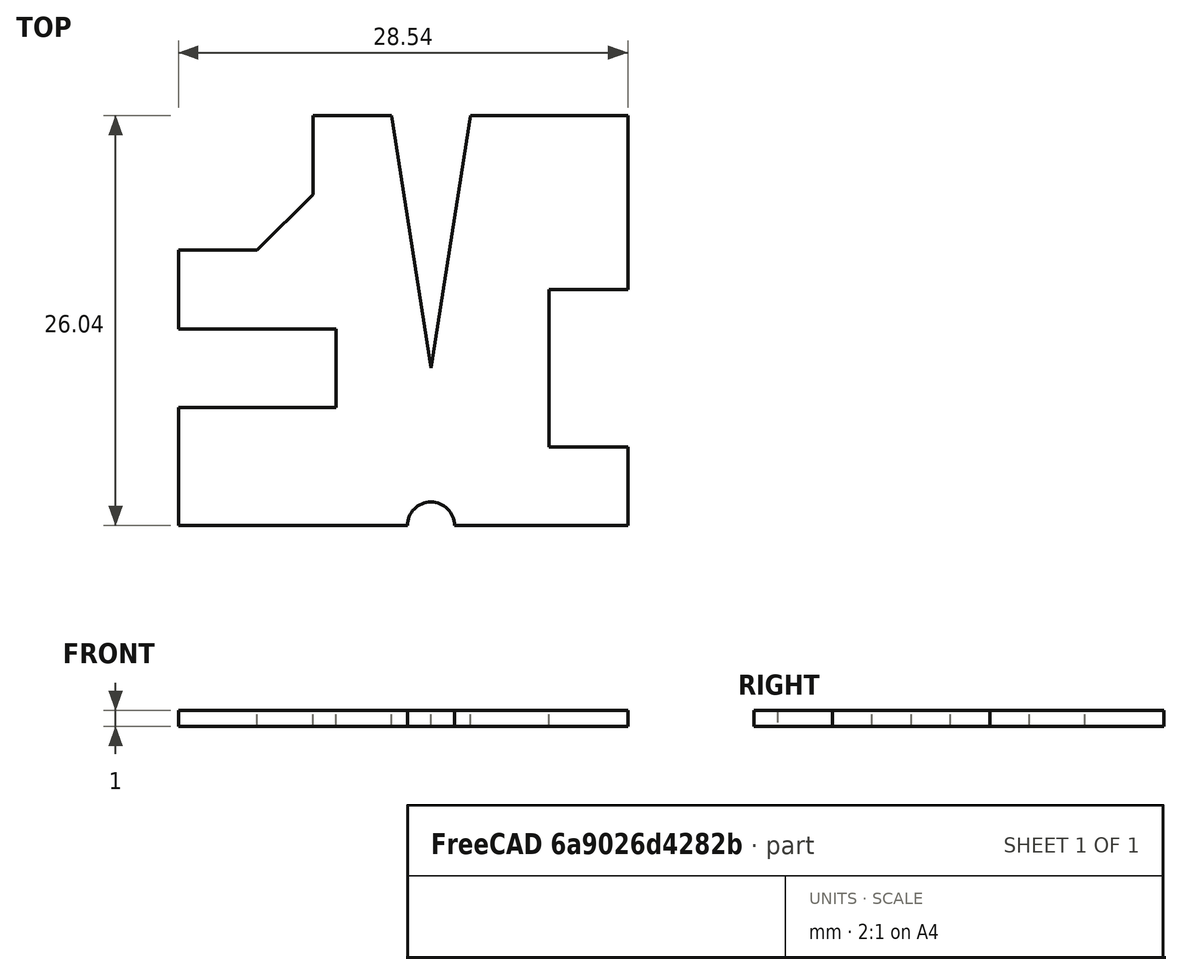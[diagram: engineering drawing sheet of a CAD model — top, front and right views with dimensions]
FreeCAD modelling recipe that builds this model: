
FCSTD DOCUMENT  (FreeCAD 0.19R16203 (Git))
Label: DogBone
License: CreativeCommons Attribution
LicenseURL: http://creativecommons.org/licenses/by/4.0/
objects: Sketcher::SketchObject×1, PartDesign::Pad×1, PartDesign::Body×1
note: 4 computed .brp shape members not serialized (recipe doc carries the construction recipe); baked Part::Feature solids carry a one-line shape summary decoded from their .brp

FEATURE [Sketcher::SketchObject] Sketch
  MapMode = 5
  Support = -> [XY_Plane001]
  sketch-geometry (20):
    g0: LineSegment StartX=-16.0355 StartY=-10 StartZ=0 EndX=-16.0355 EndY=-2.5 EndZ=0
    g1: LineSegment StartX=-16.0355 StartY=-2.5 StartZ=0 EndX=-6.03553 EndY=-2.5 EndZ=0
    g2: LineSegment StartX=-6.03553 StartY=-2.5 StartZ=0 EndX=-6.03553 EndY=2.5 EndZ=0
    g3: LineSegment StartX=-6.03553 StartY=2.5 StartZ=0 EndX=-16.0355 EndY=2.5 EndZ=0
    g4: LineSegment StartX=-16.0355 StartY=2.5 StartZ=0 EndX=-16.0355 EndY=7.5 EndZ=0
    g5: LineSegment StartX=-16.0355 StartY=7.5 StartZ=0 EndX=-11.0355 EndY=7.5 EndZ=0
    g6: LineSegment StartX=-11.0355 StartY=7.5 StartZ=0 EndX=-7.5 EndY=11.0355 EndZ=0
    g7: LineSegment StartX=-7.5 StartY=11.0355 StartZ=0 EndX=-7.5 EndY=16.0355 EndZ=0
    g8: LineSegment StartX=-7.5 StartY=16.0355 StartZ=0 EndX=-2.5 EndY=16.0355 EndZ=0
    g9: LineSegment StartX=-2.5 StartY=16.0355 StartZ=0 EndX=0 EndY=0 EndZ=0
    g10: LineSegment StartX=0 StartY=0 StartZ=0 EndX=2.5 EndY=16.0355 EndZ=0
    g11: LineSegment StartX=2.5 StartY=16.0355 StartZ=0 EndX=12.5 EndY=16.0355 EndZ=0
    g12: LineSegment StartX=12.5 StartY=16.0355 StartZ=0 EndX=12.5 EndY=5 EndZ=0
    g13: LineSegment StartX=12.5 StartY=5 StartZ=0 EndX=7.5 EndY=5 EndZ=0
    g14: LineSegment StartX=7.5 StartY=5 StartZ=0 EndX=7.5 EndY=-5 EndZ=0
    g15: LineSegment StartX=7.5 StartY=-5 StartZ=0 EndX=12.5 EndY=-5 EndZ=0
    g16: LineSegment StartX=12.5 StartY=-5 StartZ=0 EndX=12.5 EndY=-10 EndZ=0
    g17: LineSegment StartX=12.5 StartY=-10 StartZ=0 EndX=1.5 EndY=-10 EndZ=0
    g18: LineSegment StartX=-1.5 StartY=-10 StartZ=0 EndX=-16.0355 EndY=-10 EndZ=0
    g19: ArcOfCircle CenterX=0 CenterY=-10 CenterZ=0 NormalX=0 NormalY=0 NormalZ=1 AngleXU=0 Radius=1.5 StartAngle=0 EndAngle=3.14159
  constraints (57):
    c: Vertical(g0)
    c: Coincident(g0,g1)
    c: Horizontal(g1)
    c: Coincident(g1,g2)
    c: Coincident(g2,g3)
    c: Horizontal(g3)
    c: Coincident(g3,g4)
    c: Vertical(g4)
    c: Coincident(g4,g5)
    c: Horizontal(g5)
    c: Coincident(g5,g6)
    c: Coincident(g6,g7)
    c: Vertical(g7)
    c: Coincident(g7,g8)
    c: Horizontal(g8)
    c: Coincident(g8,g9)
    c: Coincident(g9,g10)
    c: Coincident(g10,g11)
    c: Horizontal(g11)
    c: Coincident(g11,g12)
    c: Vertical(g12)
    c: Coincident(g12,g13)
    c: Coincident(g13,g14)
    c: Coincident(g14,g15)
    c: Horizontal(g15)
    c: Coincident(g15,g16)
    c: Vertical(g16)
    c: Coincident(g18,g0)
    c: Horizontal(g13)
    c: Equal(g13,g15)
    c: Symmetric(g13,g14,g-1)
    c: Symmetric(g8,g10,g-2)
    c: Equal(g3,g1)
    c: Symmetric(g3,g0,g-1)
    c: DistanceX(g15,g15) = 5
    c: Angle(g6) = 0.785398
    c: DistanceY(g14,g14) = 10
    c: DistanceX(g8,g10) = 5
    c: DistanceY(g2,g2) = 5
    c: Distance(g6) = 5
    c: DistanceX(g5,g5) = 5
    c: DistanceY(g7,g7) = 5
    c: DistanceY(g4,g4) = 5
    c: DistanceX(g8,g8) = 5
    c: DistanceX(g3,g3) = 10
    c: DistanceX(g11,g11) = 10
    c: Coincident(g9,g-1)
    c: DistanceY(g16,g16) = 5
    c: PointOnObject(g19,g-2)
    c: PointOnObject(g19,g17)
    c: Coincident(g19,g17)
    c: Coincident(g18,g19)
    c: Symmetric(g17,g18,g19)
    c: Radius(g19) = 1.5
    c: Horizontal(g17)
    c: Horizontal(g18)
    c: Coincident(g17,g16)
FEATURE [PartDesign::Pad] Pad
  Length = 1
  Length2 = 100
  Profile = -> Sketch
  Type = 0
FEATURE [PartDesign::Body] PadBody  label="DogBone"
  Group = -> [Sketch,Pad]
  Origin = -> Origin001
  Tip = -> Pad
